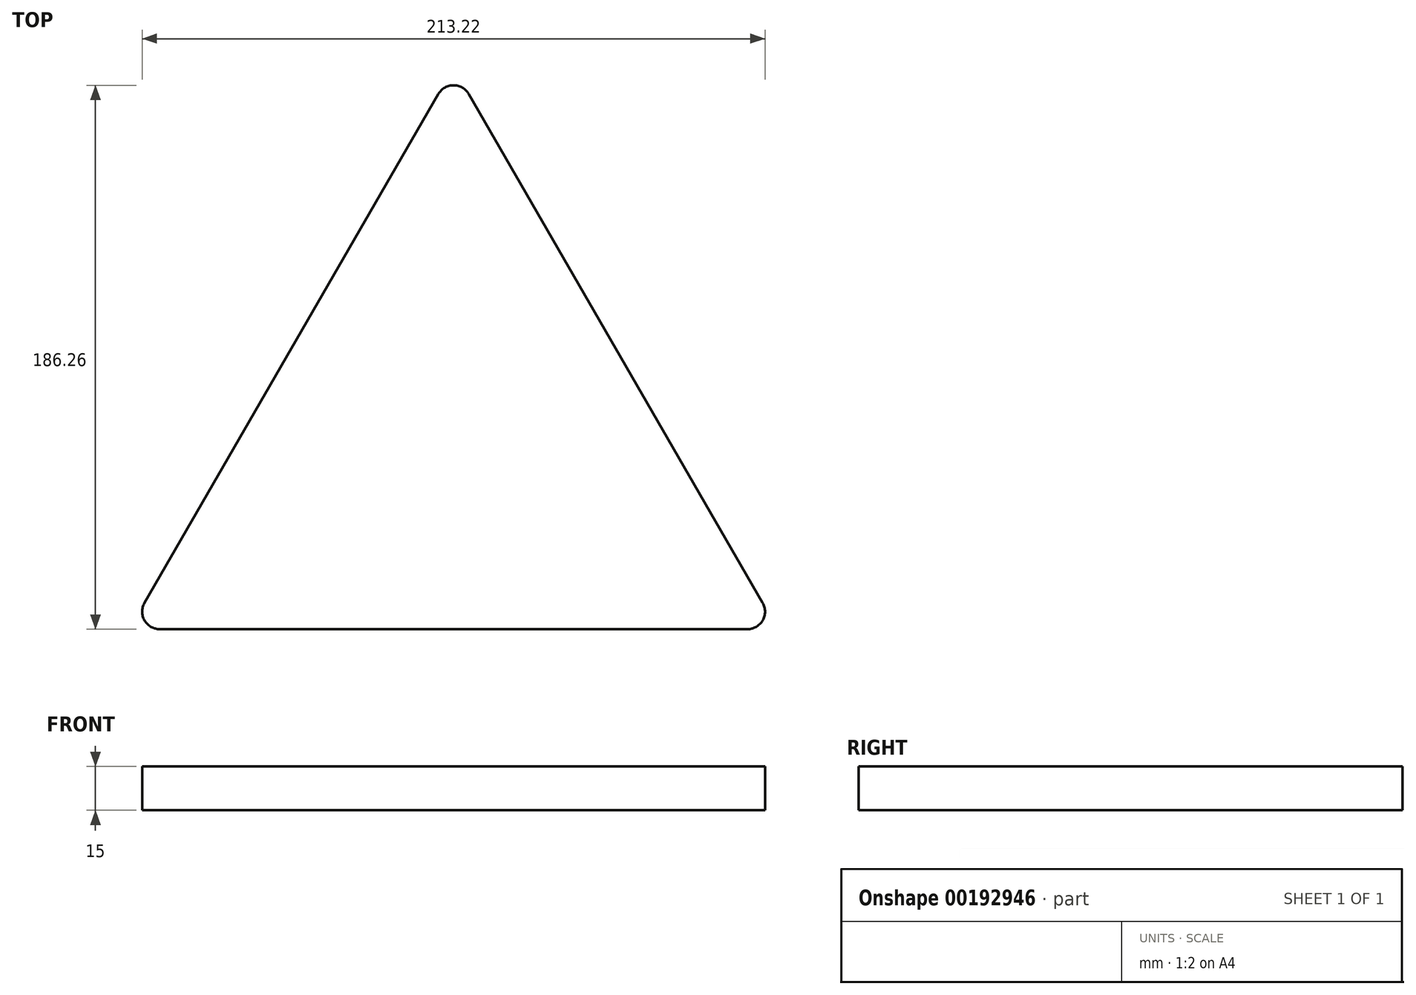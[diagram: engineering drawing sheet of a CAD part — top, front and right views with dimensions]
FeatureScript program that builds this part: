
annotation { "Feature Type Name" : "Feature", "Feature Type Description" : "" }
export const myFeature = defineFeature(function(context is Context, id is Id, definition is map)
    precondition{}
    {
        {
            var Q0;
            Q0=qCreatedBy(makeId("Top.planeOp"),FACE);
            var sketch = newSketch(context, id + "F0", { "sketchPlane" : qUnion([Q0])});
            skLineSegment(sketch, "E0", {"start": v(-5.2, -9) * mm, "end": v(-105.8, -183.26) * mm});
            skLineSegment(sketch, "E1", {"start": v(-100.6, -192.26) * mm, "end": v(100.6, -192.26) * mm});
            skLineSegment(sketch, "E2", {"start": v(105.8, -183.26) * mm, "end": v(5.2, -9) * mm});
            skPoint(sketch, "E3.visualSharp", {"position": v(-111, -192.26) * mm});
            skArc(sketch, "E3.filletArc", {"start": v(-105.8, -183.26) * mm, "mid": v(-105.8, -189.26) * mm, "end": v(-100.6, -192.26) * mm});
            skPoint(sketch, "E4.visualSharp", {"position": v(111, -192.26) * mm});
            skArc(sketch, "E4.filletArc", {"start": v(100.6, -192.26) * mm, "mid": v(105.8, -189.26) * mm, "end": v(105.8, -183.26) * mm});
            skPoint(sketch, "E5.visualSharp", {"position": v(0, 0) * mm});
            skArc(sketch, "E5.filletArc", {"start": v(5.2, -9) * mm, "mid": v(0, -6) * mm, "end": v(-5.2, -9) * mm});
            skSolve(sketch);
        }
        {
            var Q0;
            Q0 = qSketchRegion(id + "F0", true);
            extrude(context, id + "F1", {"entities" : qUnion([Q0]), "depth" : 15 * mm});
        }
    });
